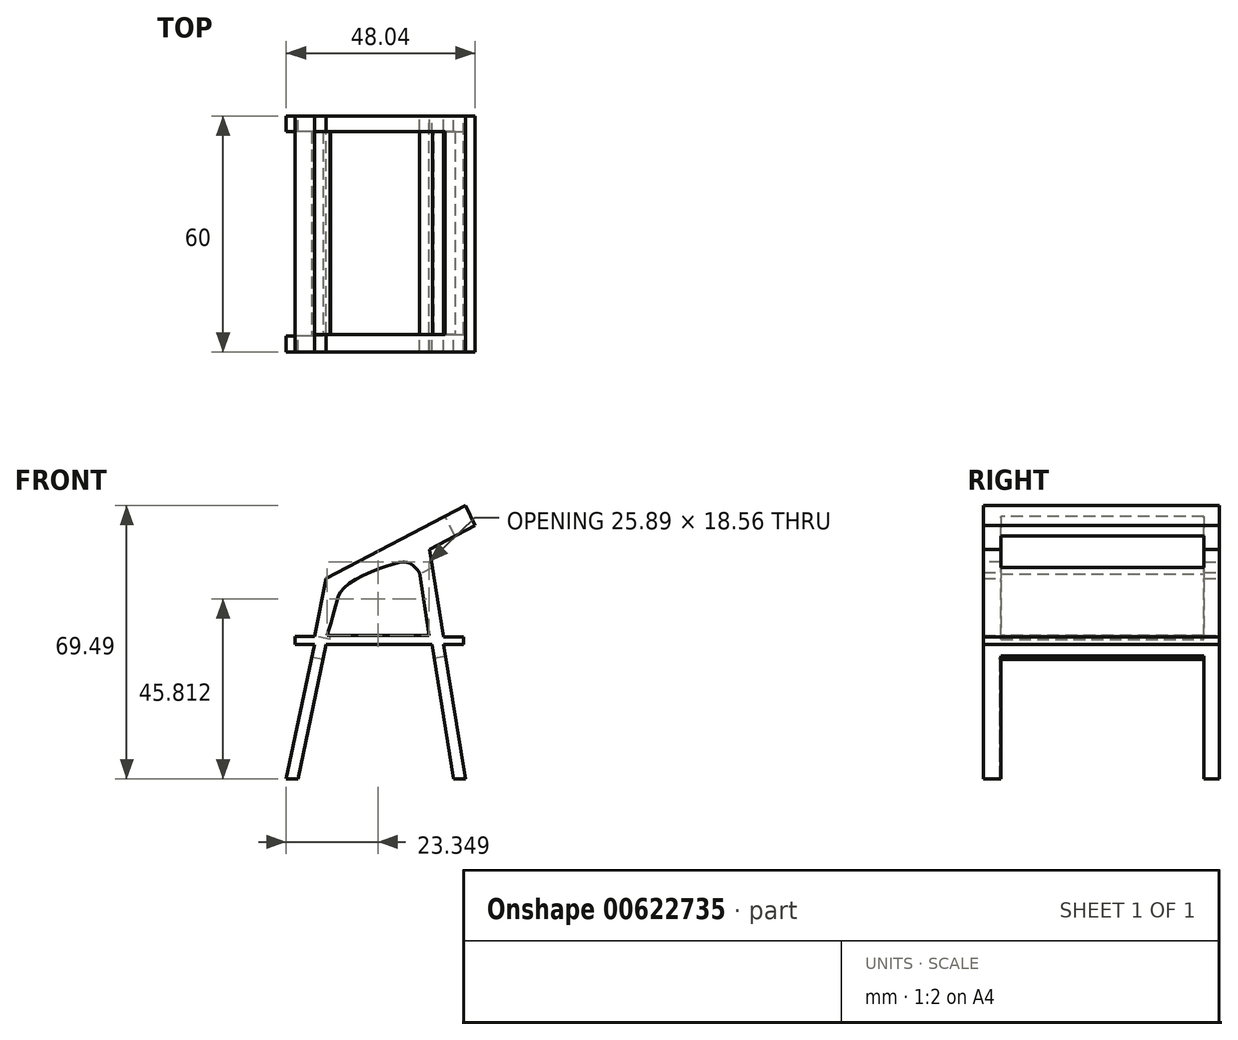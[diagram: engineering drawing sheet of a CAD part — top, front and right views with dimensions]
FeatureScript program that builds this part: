
annotation { "Feature Type Name" : "Feature", "Feature Type Description" : "" }
export const myFeature = defineFeature(function(context is Context, id is Id, definition is map)
    precondition{}
    {
        {
            var Q0;
            Q0=qCreatedBy(makeId("Front.planeOp"),FACE);
            var sketch = newSketch(context, id + "F0", { "sketchPlane" : qUnion([Q0])});
            skLineSegment(sketch, "E0", {"start": v(-20.34, 25.46) * mm, "end": v(-55.8, 6.93) * mm});
            skLineSegment(sketch, "E1", {"start": v(-55.8, 6.93) * mm, "end": v(-58.73, -7.78) * mm});
            skLineSegment(sketch, "E2", {"start": v(-58.73, -7.78) * mm, "end": v(-63.73, -7.78) * mm});
            skLineSegment(sketch, "E3", {"start": v(-63.73, -7.78) * mm, "end": v(-63.73, -9.78) * mm});
            skLineSegment(sketch, "E4", {"start": v(-63.73, -9.78) * mm, "end": v(-58.73, -9.78) * mm});
            skLineSegment(sketch, "E5", {"start": v(-58.73, -9.78) * mm, "end": v(-65.93, -44.03) * mm});
            skLineSegment(sketch, "E6", {"start": v(-65.93, -44.03) * mm, "end": v(-62.93, -44.03) * mm});
            skLineSegment(sketch, "E7", {"start": v(-62.93, -44.03) * mm, "end": v(-55.8, -9.78) * mm});
            skLineSegment(sketch, "E8", {"start": v(-55.8, -9.78) * mm, "end": v(-28.91, -9.78) * mm});
            skLineSegment(sketch, "E9", {"start": v(-28.91, -9.78) * mm, "end": v(-23.35, -44.03) * mm});
            skLineSegment(sketch, "E10", {"start": v(-23.35, -44.03) * mm, "end": v(-20.35, -44.03) * mm});
            skLineSegment(sketch, "E11", {"start": v(-20.35, -44.03) * mm, "end": v(-25.9, -9.9) * mm});
            skLineSegment(sketch, "E12", {"start": v(-25.9, -9.9) * mm, "end": v(-20.9, -9.9) * mm});
            skLineSegment(sketch, "E13", {"start": v(-20.9, -9.9) * mm, "end": v(-20.9, -7.9) * mm});
            skLineSegment(sketch, "E14", {"start": v(-20.9, -7.9) * mm, "end": v(-25.9, -7.9) * mm});
            skLineSegment(sketch, "E15", {"start": v(-25.9, -7.9) * mm, "end": v(-29.5, 14.25) * mm});
            skLineSegment(sketch, "E16", {"start": v(-29.5, 14.25) * mm, "end": v(-20.64, 18.91) * mm});
            skLineSegment(sketch, "E17", {"start": v(-20.64, 18.91) * mm, "end": v(-17.9, 20.36) * mm});
            skLineSegment(sketch, "E18", {"start": v(-20.34, 25.46) * mm, "end": v(-17.9, 20.36) * mm});
            skSolve(sketch);
        }
        {
            var Q0;
            Q0=qCreatedBy(makeId("Front.planeOp"),FACE);
            var sketch = newSketch(context, id + "F1", { "sketchPlane" : qUnion([Q0])});
            skLineSegment(sketch, "E19", {"start": v(-55.52, -7.5) * mm, "end": v(-29.64, -7.5) * mm});
            skLineSegment(sketch, "E20", {"start": v(-29.64, -7.5) * mm, "end": v(-32.06, 8.47) * mm});
            skFitSpline(sketch, "E21", {"points": [v(-32.06, 8.47) * mm, v(-34.72, 10.89) * mm, v(-38.59, 10.65) * mm, v(-50.93, 4.84) * mm, v(-53.35, 0) * mm, v(-55.52, -7.5) * mm], "startDerivative": vector(-17.28, 19.9) * mm, "endDerivative": vector(-11.07, -36.12) * mm});
            skSolve(sketch);
        }
        {
            var Q0;
            Q0=makeQuery(id+"F0.imprint","IMPRINT",FACE,{"disambiguationData":[TD([[makeQuery(id+"F0.imprint","IMPRINT",EDGE,{"derivedFrom":sQuery(id+"F0.wireOp",EDGE,"E0")}),1.0]])]});
            var Q1;
            Q1 = qSketchRegion(id + "F0", true);
            extrude(context, id + "F2", {"entities" : qUnion([Q0, Q1]), "depth" : 60 * mm, "offsetDistance" : 25 * mm});
        }
        {
            var Q0;
            Q0=makeQuery(id+"F1.imprint","IMPRINT",FACE,{"disambiguationData":[TD([[makeQuery(id+"F1.imprint","IMPRINT",EDGE,{"derivedFrom":sQuery(id+"F1.wireOp",EDGE,"E19")}),1.0]])]});
            extrude(context, id + "F3", {"entities" : qUnion([Q0]), "operationType" : NewBodyOperationType.REMOVE, "depth" : 60 * mm, "offsetDistance" : 25 * mm});
        }
        {
            var Q0;
            Q0=makeQuery(id+"F2.opExtrude","SWEPT_FACE",FACE,{"disambiguationData":[OSD([sQuery(id+"F0.wireOp",EDGE,"E0")])]});
            var sketch = newSketch(context, id + "F4", { "sketchPlane" : qUnion([Q0])});
            skLineSegment(sketch, "E22.bottom", {"start": v(-12.17, -3.98) * mm, "end": v(-46.24, -3.98) * mm});
            skLineSegment(sketch, "E22.top", {"start": v(-12.17, -55.52) * mm, "end": v(-46.24, -55.52) * mm});
            skLineSegment(sketch, "E22.left", {"start": v(-12.17, -3.98) * mm, "end": v(-12.17, -55.52) * mm});
            skLineSegment(sketch, "E22.right", {"start": v(-46.24, -3.98) * mm, "end": v(-46.24, -55.52) * mm});
            skSolve(sketch);
        }
        {
            var Q0;
            Q0=makeQuery(id+"F4.imprint","IMPRINT",FACE,{"disambiguationData":[TD([[makeQuery(id+"F4.imprint","IMPRINT",EDGE,{"derivedFrom":sQuery(id+"F4.wireOp",EDGE,"E22.bottom")}),1.0]])]});
            extrude(context, id + "F5", {"entities" : qUnion([Q0]), "operationType" : NewBodyOperationType.REMOVE, "oppositeDirection" : true, "depth" : 10 * mm, "offsetDistance" : 25 * mm});
        }
        {
            var Q0;
            Q0=makeQuery(id+"F2.opExtrude","SWEPT_FACE",FACE,{"disambiguationData":[OSD([sQuery(id+"F0.wireOp",EDGE,"E1")])]});
            var sketch = newSketch(context, id + "F6", { "sketchPlane" : qUnion([Q0])});
            skLineSegment(sketch, "E23.bottom", {"start": v(3.98, -19.15) * mm, "end": v(55.52, -19.15) * mm});
            skLineSegment(sketch, "E23.top", {"start": v(3.98, -4.15) * mm, "end": v(55.52, -4.15) * mm});
            skLineSegment(sketch, "E23.left", {"start": v(3.98, -19.15) * mm, "end": v(3.98, -4.15) * mm});
            skLineSegment(sketch, "E23.right", {"start": v(55.52, -19.15) * mm, "end": v(55.52, -4.15) * mm});
            skSolve(sketch);
        }
        {
            var Q0;
            Q0=makeQuery(id+"F6.imprint","IMPRINT",FACE,{"disambiguationData":[TD([[makeQuery(id+"F6.imprint","IMPRINT",EDGE,{"derivedFrom":sQuery(id+"F6.wireOp",EDGE,"E23.bottom")}),-1.0]])]});
            var Q1;
            Q1=sQuery(id+"F6.wireOp",EDGE,"E23.bottom");
            extrude(context, id + "F7", {"entities" : qUnion([Q0]), "operationType" : NewBodyOperationType.REMOVE, "surfaceEntities" : qUnion([Q1]), "oppositeDirection" : true, "depth" : 4 * mm, "offsetDistance" : 25 * mm});
        }
        {
            var Q0;
            Q0=makeQuery(id+"F2.opExtrude","SWEPT_FACE",FACE,{"disambiguationData":[OSD([sQuery(id+"F0.wireOp",EDGE,"E5")])]});
            var sketch = newSketch(context, id + "F8", { "sketchPlane" : qUnion([Q0])});
            skLineSegment(sketch, "E24.bottom", {"start": v(4.01, -25.02) * mm, "end": v(55.99, -25.02) * mm});
            skLineSegment(sketch, "E24.top", {"start": v(4.01, -62.28) * mm, "end": v(55.99, -62.28) * mm});
            skLineSegment(sketch, "E24.left", {"start": v(4.01, -25.02) * mm, "end": v(4.01, -62.28) * mm});
            skLineSegment(sketch, "E24.right", {"start": v(55.99, -25.02) * mm, "end": v(55.99, -62.28) * mm});
            skSolve(sketch);
        }
        {
            var Q0;
            {var subQ0=sQuery(id+"F8.wireOp",EDGE,"E24.bottom");Q0=makeQuery(id+"F8.imprint","IMPRINT",FACE,{"disambiguationData":[TD([[makeQuery(id+"F8.imprint","IMPRINT",EDGE,{"derivedFrom":subQ0}),-1.0]])]});}
            extrude(context, id + "F9", {"entities" : qUnion([Q0]), "operationType" : NewBodyOperationType.REMOVE, "oppositeDirection" : true, "depth" : 15 * mm, "offsetDistance" : 25 * mm});
        }
        {
            var Q0;
            Q0=makeQuery(id+"F2.opExtrude","SWEPT_FACE",FACE,{"disambiguationData":[OSD([sQuery(id+"F0.wireOp",EDGE,"E11")])]});
            var sketch = newSketch(context, id + "F10", { "sketchPlane" : qUnion([Q0])});
            skLineSegment(sketch, "E25.bottom", {"start": v(-55.51, -8.55) * mm, "end": v(-4.01, -8.55) * mm});
            skLineSegment(sketch, "E25.top", {"start": v(-55.51, -43.91) * mm, "end": v(-4.01, -43.91) * mm});
            skLineSegment(sketch, "E25.left", {"start": v(-55.51, -8.55) * mm, "end": v(-55.51, -43.91) * mm});
            skLineSegment(sketch, "E25.right", {"start": v(-4.01, -8.55) * mm, "end": v(-4.01, -43.91) * mm});
            skSolve(sketch);
        }
        {
            var Q0;
            {var subQ0=sQuery(id+"F10.wireOp",EDGE,"E25.bottom");Q0=makeQuery(id+"F10.imprint","IMPRINT",FACE,{"disambiguationData":[TD([[makeQuery(id+"F10.imprint","IMPRINT",EDGE,{"derivedFrom":subQ0}),-1.0]])]});}
            extrude(context, id + "F11", {"entities" : qUnion([Q0]), "operationType" : NewBodyOperationType.REMOVE, "oppositeDirection" : true, "depth" : 6.8 * mm, "offsetDistance" : 25 * mm});
        }
    });
